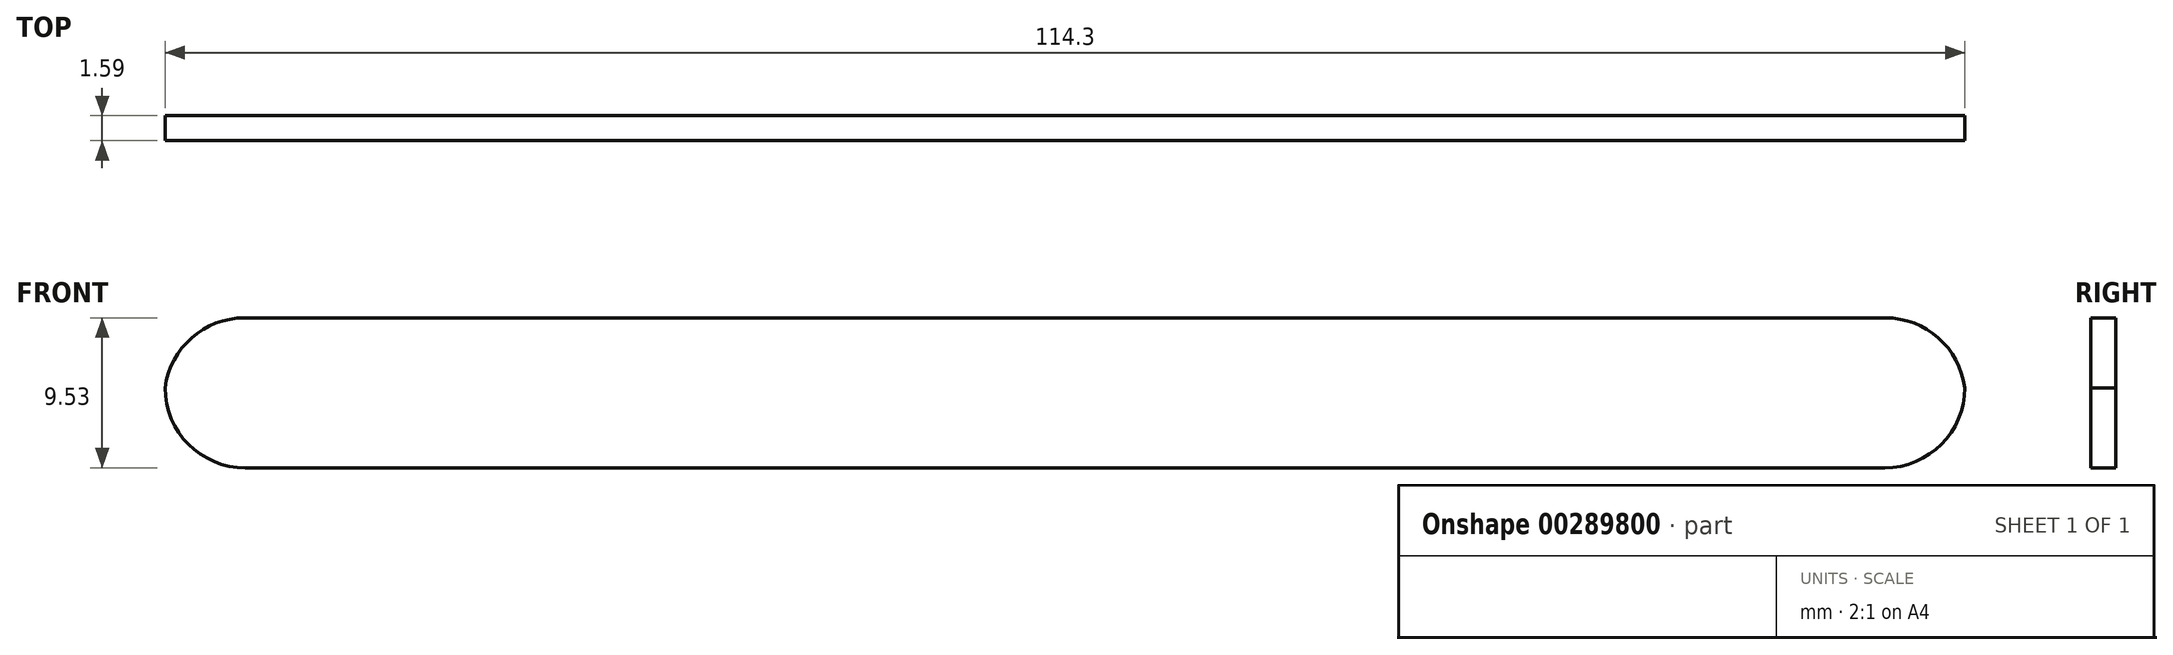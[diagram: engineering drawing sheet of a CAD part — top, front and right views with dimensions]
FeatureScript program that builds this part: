
annotation { "Feature Type Name" : "Feature", "Feature Type Description" : "" }
export const myFeature = defineFeature(function(context is Context, id is Id, definition is map)
    precondition{}
    {
        {
            var Q0;
            Q0=qCreatedBy(makeId("Front.planeOp"),FACE);
            var sketch = newSketch(context, id + "F0", { "sketchPlane" : qUnion([Q0])});
            skLineSegment(sketch, "E0.bottom", {"start": v(-64.92, 18.44) * mm, "end": v(49.38, 18.44) * mm});
            skLineSegment(sketch, "E0.top", {"start": v(-64.92, 27.97) * mm, "end": v(49.38, 27.97) * mm});
            skLineSegment(sketch, "E0.left", {"start": v(-64.92, 18.44) * mm, "end": v(-64.92, 27.97) * mm});
            skLineSegment(sketch, "E0.right", {"start": v(49.38, 18.44) * mm, "end": v(49.38, 27.97) * mm});
            skSolve(sketch);
        }
        {
            var Q0;
            Q0=makeQuery(id+"F0.imprint","IMPRINT",FACE,{"disambiguationData":[TD([[makeQuery(id+"F0.imprint","IMPRINT",EDGE,{"derivedFrom":sQuery(id+"F0.wireOp",EDGE,"E0.bottom")}),1.0]])]});
            extrude(context, id + "F1", {"entities" : qUnion([Q0]), "depth" : 1.59 * mm});
        }
        {
            var Q0;
            Q0=makeQuery(id+"F1.opExtrude","SWEPT_EDGE",EDGE,{"disambiguationData":[OSD([sQuery(id+"F0.wireOp",EDGE,"E0.bottom"),sQuery(id+"F0.wireOp",EDGE,"E0.left")])]});
            fillet(context, id + "F2", {"entities" : qUnion([Q0]), "radius" : 5.08 * mm, "tangentPropagation" : true, "allowEdgeOverflow" : false});
        }
        {
            var Q0;
            Q0=makeQuery(id+"F1.opExtrude","SWEPT_EDGE",EDGE,{"disambiguationData":[OSD([sQuery(id+"F0.wireOp",EDGE,"E0.top"),sQuery(id+"F0.wireOp",EDGE,"E0.left")])]});
            fillet(context, id + "F3", {"entities" : qUnion([Q0]), "radius" : 5.08 * mm, "tangentPropagation" : true, "allowEdgeOverflow" : false});
        }
        {
            var Q0;
            Q0=makeQuery(id+"F1.opExtrude","SWEPT_EDGE",EDGE,{"disambiguationData":[OSD([sQuery(id+"F0.wireOp",EDGE,"E0.bottom"),sQuery(id+"F0.wireOp",EDGE,"E0.right")])]});
            fillet(context, id + "F4", {"entities" : qUnion([Q0]), "radius" : 5.08 * mm, "tangentPropagation" : true, "allowEdgeOverflow" : false});
        }
        {
            var Q0;
            Q0=makeQuery(id+"F1.opExtrude","SWEPT_EDGE",EDGE,{"disambiguationData":[OSD([sQuery(id+"F0.wireOp",EDGE,"E0.top"),sQuery(id+"F0.wireOp",EDGE,"E0.right")])]});
            fillet(context, id + "F5", {"entities" : qUnion([Q0]), "radius" : 5.08 * mm, "tangentPropagation" : true, "allowEdgeOverflow" : false});
        }
    });
